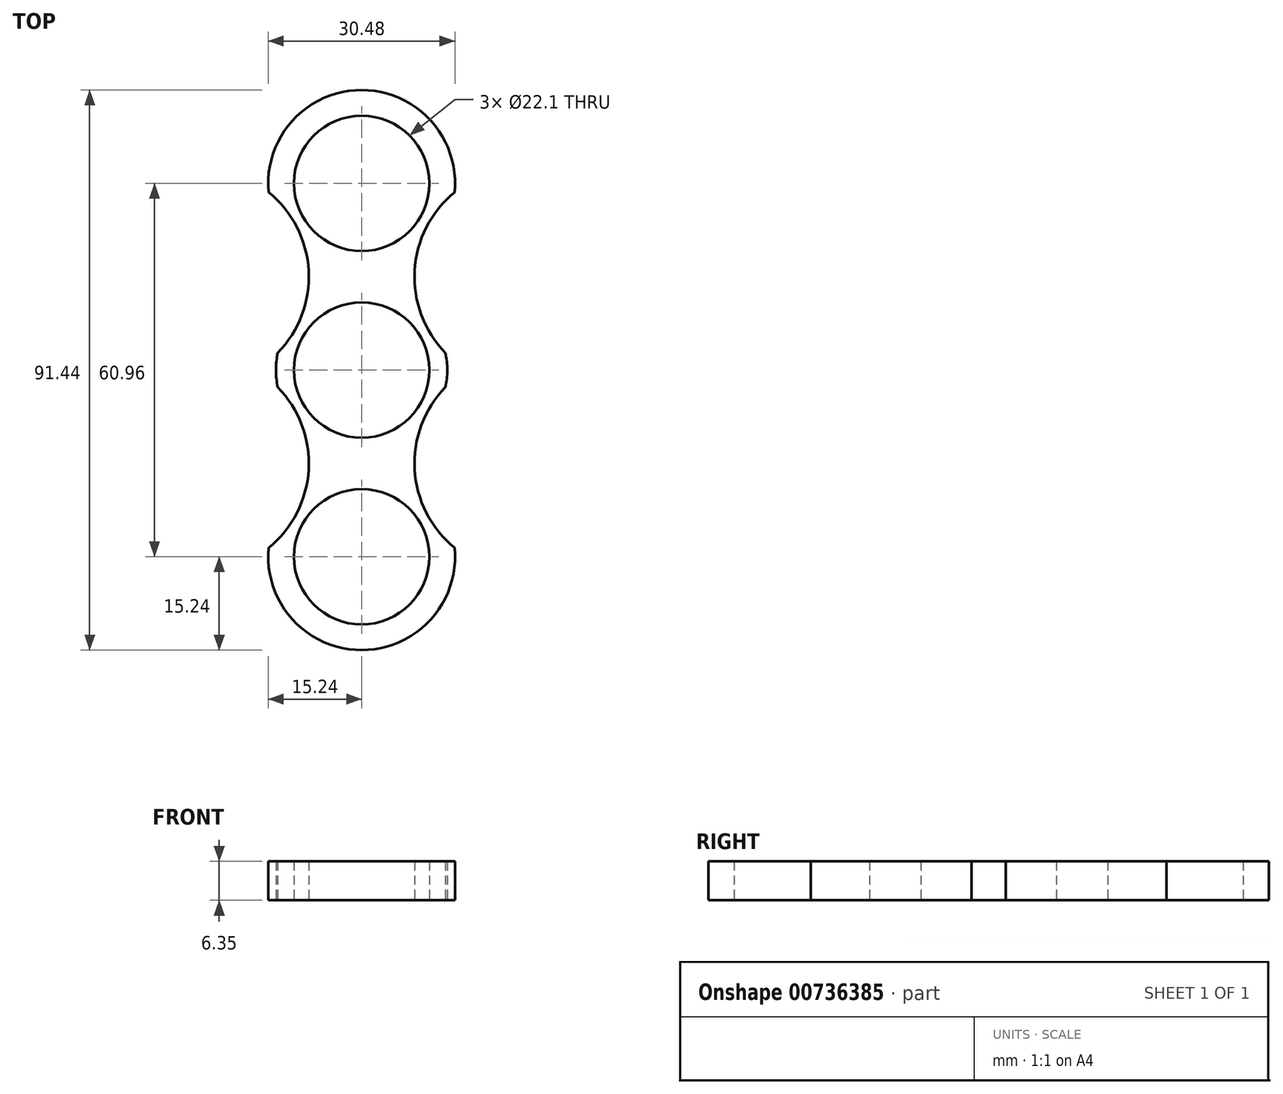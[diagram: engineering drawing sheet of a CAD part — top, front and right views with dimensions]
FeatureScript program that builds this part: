
annotation { "Feature Type Name" : "Feature", "Feature Type Description" : "" }
export const myFeature = defineFeature(function(context is Context, id is Id, definition is map)
    precondition{}
    {
        {
            var Q0;
            Q0=qCreatedBy(makeId("Top.planeOp"),FACE);
            var sketch = newSketch(context, id + "F0", { "sketchPlane" : qUnion([Q0])});
            skCircle(sketch, "E0", {"center": v(0, 0) * mm, "radius": 11.05 * mm});
            skArc(sketch, "E1", {"start": v(9.27, 10.45) * mm, "mid": v(0, 13.97) * mm, "end": v(-9.27, 10.45) * mm});
            skLineSegment(sketch, "E2", {"start": v(0, 0) * mm, "end": v(0, 30.48) * mm});
            skCircle(sketch, "E3", {"center": v(0, 30.48) * mm, "radius": 11.05 * mm});
            skArc(sketch, "E4", {"start": v(15.17, 29.03) * mm, "mid": v(0, 45.72) * mm, "end": v(-15.17, 29.03) * mm});
            skLineSegment(sketch, "E5", {"start": v(0, 0) * mm, "end": v(0, -30.48) * mm});
            skCircle(sketch, "E6", {"center": v(0, -30.48) * mm, "radius": 11.05 * mm});
            skArc(sketch, "E7", {"start": v(8.84, -18.07) * mm, "mid": v(0, -15.24) * mm, "end": v(-8.84, -18.07) * mm});
            skArc(sketch, "E8", {"start": v(13.68, -2.8) * mm, "mid": v(8.64, -16.25) * mm, "end": v(15.17, -29.03) * mm});
            skArc(sketch, "E9", {"start": v(15.17, 29.03) * mm, "mid": v(8.64, 16.25) * mm, "end": v(13.68, 2.8) * mm});
            skArc(sketch, "E10.trimOffspring", {"start": v(13.68, -2.8) * mm, "mid": v(13.97, 0) * mm, "end": v(13.68, 2.8) * mm});
            skArc(sketch, "E11", {"start": v(-13.68, 2.8) * mm, "mid": v(-8.64, 16.25) * mm, "end": v(-15.17, 29.03) * mm});
            skArc(sketch, "E12", {"start": v(-15.17, -29.03) * mm, "mid": v(-8.64, -16.25) * mm, "end": v(-13.68, -2.8) * mm});
            skArc(sketch, "E13.trimOffspring", {"start": v(-15.17, -29.03) * mm, "mid": v(0, -45.72) * mm, "end": v(15.17, -29.03) * mm});
            skArc(sketch, "E14.trimOffspring", {"start": v(-8.84, 18.07) * mm, "mid": v(0, 15.24) * mm, "end": v(8.84, 18.07) * mm});
            skArc(sketch, "E15.trimOffspring", {"start": v(-9.27, -10.45) * mm, "mid": v(0, -13.97) * mm, "end": v(9.27, -10.45) * mm});
            skArc(sketch, "E16.trimOffspring", {"start": v(-13.68, 2.8) * mm, "mid": v(-13.97, 0) * mm, "end": v(-13.68, -2.8) * mm});
            skSolve(sketch);
        }
        {
            var Q0;
            Q0=makeQuery(id+"F0.imprint","IMPRINT",FACE,{"disambiguationData":[TD([[makeQuery(id+"F0.imprint","IMPRINT",EDGE,{"derivedFrom":sQuery(id+"F0.wireOp",EDGE,"E3")}),-1.0]])]});
            var Q1;
            {var subQ0=sQuery(id+"F0.wireOp",EDGE,"E9");var subQ1=sQuery(id+"F0.wireOp",EDGE,"E1");var subQ2=makeQuery(id+"F0.imprint","INTERSECT",VERTEX,{"derivedFrom":[subQ1,subQ0]});Q1=makeQuery(id+"F0.imprint","IMPRINT",FACE,{"disambiguationData":[TD([[makeQuery(id+"F0.imprint","IMPRINT",EDGE,{"disambiguationData":[TD([[subQ2,-1.0]])],"derivedFrom":subQ1}),-1.0]])]});}
            var Q2;
            {var subQ0=sQuery(id+"F0.wireOp",EDGE,"E11");var subQ1=sQuery(id+"F0.wireOp",EDGE,"E1");var subQ2=makeQuery(id+"F0.imprint","INTERSECT",VERTEX,{"derivedFrom":[subQ1,subQ0]});Q2=makeQuery(id+"F0.imprint","IMPRINT",FACE,{"disambiguationData":[TD([[makeQuery(id+"F0.imprint","IMPRINT",EDGE,{"disambiguationData":[TD([[subQ2,1.0]])],"derivedFrom":subQ1}),-1.0]])]});}
            var Q3;
            {var subQ11=sQuery(id+"F0.wireOp",EDGE,"E16.trimOffspring");Q3=makeQuery(id+"F0.imprint","IMPRINT",FACE,{"disambiguationData":[TD([[makeQuery(id+"F0.imprint","IMPRINT",EDGE,{"derivedFrom":subQ11}),1.0]])]});}
            var Q4;
            {var subQ5=sQuery(id+"F0.wireOp",EDGE,"E10.trimOffspring");Q4=makeQuery(id+"F0.imprint","IMPRINT",FACE,{"disambiguationData":[TD([[makeQuery(id+"F0.imprint","IMPRINT",EDGE,{"derivedFrom":subQ5}),1.0]])]});}
            var Q5;
            {var subQ0=sQuery(id+"F0.wireOp",EDGE,"E7");var subQ1=sQuery(id+"F0.wireOp",EDGE,"E5");var subQ2=makeQuery(id+"F0.imprint","INTERSECT",VERTEX,{"derivedFrom":[subQ1,subQ0]});Q5=makeQuery(id+"F0.imprint","IMPRINT",FACE,{"disambiguationData":[TD([[makeQuery(id+"F0.imprint","IMPRINT",EDGE,{"disambiguationData":[TD([[subQ2,1.0]])],"derivedFrom":subQ1}),1.0]])]});}
            var Q6;
            {var subQ0=sQuery(id+"F0.wireOp",EDGE,"E7");var subQ1=sQuery(id+"F0.wireOp",EDGE,"E5");var subQ2=makeQuery(id+"F0.imprint","INTERSECT",VERTEX,{"derivedFrom":[subQ1,subQ0]});Q6=makeQuery(id+"F0.imprint","IMPRINT",FACE,{"disambiguationData":[TD([[makeQuery(id+"F0.imprint","IMPRINT",EDGE,{"disambiguationData":[TD([[subQ2,1.0]])],"derivedFrom":subQ1}),-1.0]])]});}
            var Q7;
            Q7=makeQuery(id+"F0.imprint","IMPRINT",FACE,{"disambiguationData":[TD([[makeQuery(id+"F0.imprint","IMPRINT",EDGE,{"derivedFrom":sQuery(id+"F0.wireOp",EDGE,"E6")}),-1.0]])]});
            extrude(context, id + "F1", {"entities" : qUnion([Q0, Q1, Q2, Q3, Q4, Q5, Q6, Q7]), "depth" : 6.35 * mm, "offsetDistance" : 25.4 * mm});
        }
    });
